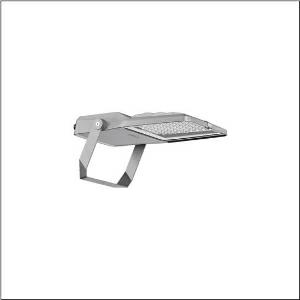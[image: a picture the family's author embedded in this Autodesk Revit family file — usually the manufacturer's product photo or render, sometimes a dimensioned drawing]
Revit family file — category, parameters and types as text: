
# Revit family: floodlight_fl_21_iq_mini___pl52_5xa7772c3d1a_c98d
name_source: partatom
category: Lighting Fixtures
units: mm (PartAtom-declared; Revit-internal decimal feet)

## family parameters
Cut with Voids When Loaded = No
Host = Face
Light Source = No
Part Type = Normal
Room Calculation Point = No
Round Connector Dimension = Use Diameter
Shared = No

## types (1)
- --- (1 x LED, 10510 lm, 87.2 W, 3000K)
    Apparent Load = 87 VA
    CIE Flux Codes = 26 60 98 100 100
    Color Rendering = 80
    Color Temperature = 3000K
    Default Elevation = 1800 mm
    Description = Floodlight FL 21 iQ mini, floodlight, primary light control with lens, of PMMA, primary optical cover: protective disc, of toughened safety glass, transparent, light distribution: PL52, light emission: direct distribution, installation type: surface-mounted, LED, High Power LED, rated luminous flux: 10.510lm, luminous efficacy: 121lm/W, light colour: 830, colour temperature: 3000K, control gear: iQ Street-Remote/DALI, control: Street-Remote, Auto-Match, Temp-Guard, Night-Set, Smart-Wire, Desk-Remote (wireless, voltage-free reading and setting of iQ features in the workshop via application-optimized NFC function/RFID function), optimised constant luminous flux control (CLO 2.0), with terminal, 6-pole, mains connection: 220..240V, AC, 50/60Hz, start of lifetime: 87W, end of service life: 92W, reduction: 40W, luminaire housing, of diecast aluminium, powder-coated, Siteco® metallic grey (DB 702S), corrosivity category C5 mid according to DIN EN ISO 12944, suitable for swimming pools, chlorine-resistant, sealing non-destructively replaceable, mounting bracket, of steel, galvanised, powder-coated, Siteco® metallic grey (DB 702S), protection rating (complete): IP66, insulation class (complete): insulation class II (safety insulation), certification: CE, ENEC, VDE, protection symbol: D, impact resistance: IK08, permissible operating ambient temperature: -40..+40°C, permissible operating ambient temperature for outdoor applications: -40..+50°C, standard: DIN EN 12944, LABS conformity tested according to VDMA 24364:2018-05, packaging unit: 1 piece

Light Distribution: PL52
    Height = 70 mm
    Lamp = 1 x LED
    Lamp Light Flux = 10510 lm
    Lamp Power = 87.2 W
    Lamp count = 1
    Length = 485 mm
    Luminous efficacy = 121 lm/W
    Manufacturer = Siteco
    ModVariant = No
    Model = 5XA7772C3D1A
    Number of Poles = 1
    OnlyDefault = Yes
    Power Factor = 1
    Product Name = Floodlight FL 21 iQ mini | PL52
    Product group = floodlight | pylon annexe
    ProductGroupID = 6201
    Protection Class = Protection class II
    Protection Degree = IP 66
    RLX_Detail_Level = 1
    RLX_Emergency_Light_Flux = 0 lm
    RLX_Emergency_Type = 0
    RLX_Emergency_Type_DB = No
    RlxData = <blob elided: 96949 chars, md5=6037db08>
    Socket = socket
    Standby Power = 0 W
    System Light Flux = 10510 lm
    System Power = 87 W
    Type Comments = factory setting: luminous flux: 100 % | dim-lin: 254 | 456 mA
    Type Image = l_1006845.jpg
    URL = http://relux.com
    VarID = @adj_185725
    Voltage = 0 V
    Weight = 0.00 kg
    Width = 337 mm

## geometry (parser evidence)
native form markers: Blend x4, Sweep x11
no freeform markers — native parametric forms only
